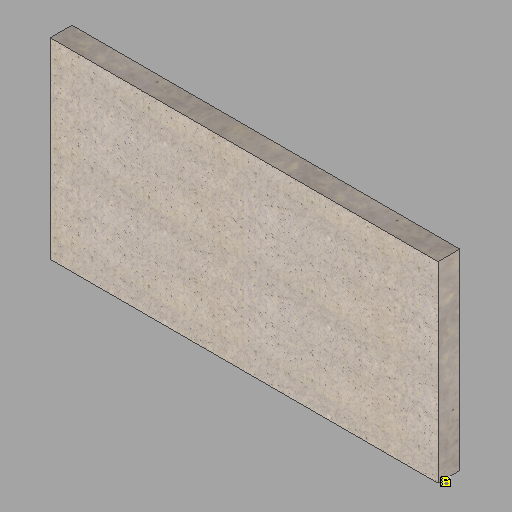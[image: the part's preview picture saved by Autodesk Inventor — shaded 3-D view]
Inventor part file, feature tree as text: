
AUTODESK INVENTOR PART (.ipt)
format: ipt  version: 2022.2 (Build 262287010, 287A)  size: 309,248 bytes
history: native  units: in
note: dims shown in document units (in); Inventor stores cm internally (conversion verified against a paired STEP export)
features: extrude x2, sketch x2
ambient origin geometry x8: Origin, YZ Plane, XZ Plane, XY Plane, X Axis, Y Axis, Z Axis, Center Point
bodies: Solid1 (feature_tree)
feature tree (4):
  extrude  "Extrusion1"  Depth=17.625in
  extrude  "Extrusion2"  Depth=2.0in
  sketch  "Sketch1"  dims[d0=35.625in d1=17.625in]
  sketch  "Sketch2"  dims[d2=2.0in d3=0.0in d4=1.25in d5=0.375in d6=0.0in d7=0.0in]
